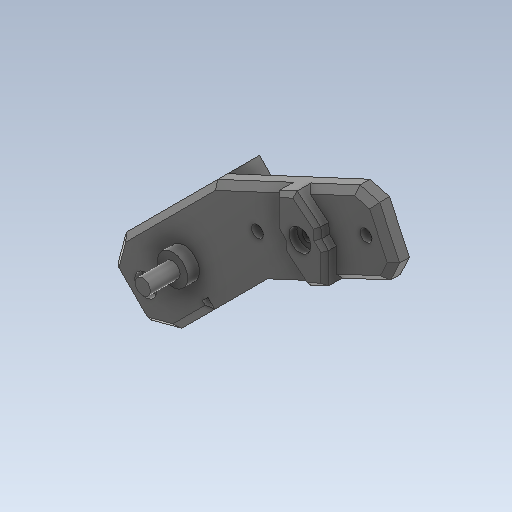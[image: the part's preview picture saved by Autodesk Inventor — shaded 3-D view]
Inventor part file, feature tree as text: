
AUTODESK INVENTOR PART (.ipt)
format: ipt  version: 2020 (Build 240168000, 168)  size: 498,688 bytes
history: native  units: in
note: dims shown in document units (in); Inventor stores cm internally (conversion verified against a paired STEP export)
features: extrude x15, sketch x15, projected_geometry x12, reference x9, other x5, chamfer x2
ambient origin geometry x8: Origin, YZ Plane, XZ Plane, XY Plane, X Axis, Y Axis, Z Axis, Center Point
bodies: Body1 (feature_tree)
feature tree (58):
  extrude  "Extrusion2"  Depth=0.7874in
  extrude  "Extrusion10"  Depth=0.3937in
  extrude  "Extrusion11"  Depth=0.7874in
  extrude  "Extrusion12"  Depth=1.5748in
  extrude  "Extrusion15"  Depth=0.1969in TaperAngle=0.0deg
  extrude  "Extrusion23"  Depth=0.1181in TaperAngle=0.0deg
  extrude  "Extrusion24"  Depth=0.2992in TaperAngle=0.0deg
  extrude  "Extrusion25"  Depth=0.5118in
  extrude  "Extrusion26"  TaperAngle=150.0deg  [1 undecoded]
  extrude  "Extrusion27"  Depth=0.315in
  extrude  "Extrusion28"  TaperAngle=120.0deg  [1 undecoded]
  extrude  "Extrusion29"  TaperAngle=90.0deg  [1 undecoded]
  extrude  "Extrusion31"  Depth=0.1181in
  extrude  "Extrusion32"  Depth=0.962in
  chamfer  "Chamfer20"  Distance=0.4724in
  chamfer  "Chamfer22"  Distance=0.0157in
  extrude  "Extrusion34"  Depth=0.3189in TaperAngle=0.0deg
  sketch  "Sketch1"  dims[d0=0.3937in d4=0.7874in]
  reference  "Reference1"
  reference  "Reference2"
  reference  "Reference3"
  reference  "Reference4"
  reference  "Reference5"
  reference  "Reference6"
  reference  "Reference7"
  sketch  "Sketch9"  dims[d46=0.2953in d47=0.0in d109=0.3937in]
  projected_geometry  "Projected Loop9"
  sketch  "Sketch10"  dims[d110=135.0deg d111=0.7874in]
  reference  "Reference8"
  sketch  "Sketch11"  dims[d114=1.0994in d115=1.5748in]
  reference  "Reference9"
  sketch  "Sketch15"  dims[d116=1.1811in d153=0.1969in d154=0.0in]
  projected_geometry  "Projected Loop11"
  sketch  "Sketch25"  dims[d155=0.0937in d156=0.1181in d157=0.0in]
  projected_geometry  "Projected Loop24"
  sketch  "Sketch26"  dims[d158=0.0039in d159=0.2992in d160=0.0in]
  projected_geometry  "Projected Loop25"
  sketch  "Sketch27"  dims[d164=0.5118in d165=0.5118in]
  projected_geometry  "Projected Loop26"
  sketch  "Sketch29"  dims[d169=150.0deg d170=150.0deg]
  projected_geometry  "Projected Loop27"
  sketch  "Sketch30"  dims[d171=0.315in d172=0.315in]
  projected_geometry  "Projected Loop28"
  sketch  "Sketch31"  dims[d173=0.4724in d174=120.0deg]
  projected_geometry  "Projected Loop29"
  sketch  "Sketch32"  dims[d175=90.0deg d176=90.0deg]
  projected_geometry  "Projected Loop30"
  sketch  "Sketch34"  dims[d184=0.8933in d185=0.1181in]
  projected_geometry  "Projected Loop34"
  projected_geometry  "Projected Loop35"
  sketch  "Sketch35"  dims[d186=180.0deg d187=0.962in]
  projected_geometry  "Projected Loop36"
  sketch  "Sketch37"  dims[d188=0.962in d189=0.4724in d190=0.0157in d191=0.0in d260=0.3189in d261=0.0in d262=0.1969in d263=0.122in d264=0.1969in d265=0.122in d266=0.2795in d267=0.0in d270=90.0deg d271=0.0in d272=0.1181in d273=0.2362in d274=90.0deg d275=0.1181in d276=0.3937in d277=0.0in d278=0.2205in d279=0.0787in d280=0.0in d281=90.0deg d282=90.0deg d283=90.0deg d284=90.0deg d285=0.1969in d286=0.1969in d287=0.0984in d288=0.0984in d289=0.0984in d291=0.7559in d292=0.7559in d293=0.7559in d295=0.7559in d296=0.0984in d297=0.0984in d298=0.0984in d299=0.0984in d300=0.0984in d305=0.1181in d306=0.0in d307=0.2205in d308=0.0787in d309=0.0in d310=90.0deg d311=0.0394in d312=0.0394in d313=0.0394in d314=0.0394in d315=0.0984in d316=0.0in d323=0.0394in d324=0.748in d325=0.0394in d326=0.1181in d327=90.0deg d328=0.0984in d329=0.0in d330=0.0394in d331=0.0in d344=0.0394in d345=0.0787in d346=45.0deg d350=0.0591in d351=0.0787in d352=45.0deg d353=0.1535in d354=0.2992in d355=0.0in d104=0.0197in d105=0.0344in d106=0.0197in d107=0.0344in d119=0.0197in d120=0.0344in d121=0.0197in d122=0.0344in d147=0.0197in d148=0.0344in d149=0.0197in d150=0.0344in d203=0.0197in d204=0.0344in d205=0.0197in d206=0.0344in d336=0.0197in d337=0.0344in d338=0.0197in d339=0.0344in]
  parser-record x1  (decoder bookkeeping rows leaked as tree rows — omitted from the tree; the rows remain in map.json)
  other  "LegDemo2.iam"
  other  "Bearing:1"
  other  "Rolling bearing GB/T 7218-1995 Type FSN 70000-Z F 623-Z:1"
  other  "servo horn 1:3"
note: 3 required parameter values undecoded (feature->parameter linkage not recoverable at this tier; creation-order binding heuristic only, values carry confidence <= 0.55)
note: 1 file-system path scrubbed to <path> (originals preserved in map.json)
